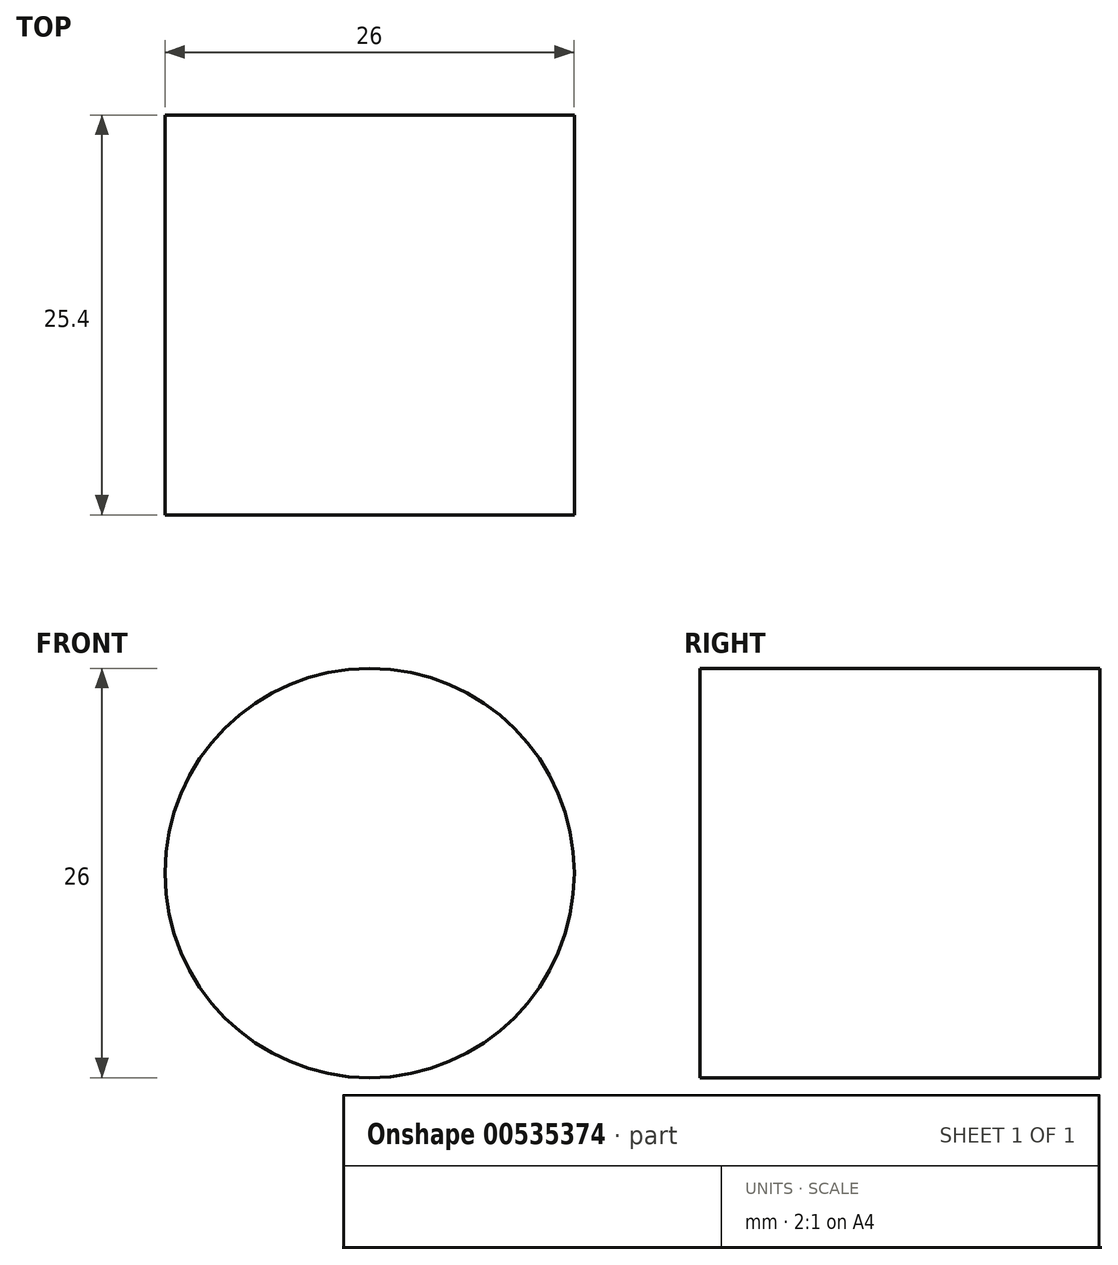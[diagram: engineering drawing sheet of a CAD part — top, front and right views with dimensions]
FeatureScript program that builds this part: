
annotation { "Feature Type Name" : "Feature", "Feature Type Description" : "" }
export const myFeature = defineFeature(function(context is Context, id is Id, definition is map)
    precondition{}
    {
        {
            var Q0;
            Q0=qCreatedBy(makeId("Front.planeOp"),FACE);
            var sketch = newSketch(context, id + "F0", { "sketchPlane" : qUnion([Q0])});
            skCircle(sketch, "E0", {"center": v(0, 0) * mm, "radius": 13 * mm});
            skSolve(sketch);
        }
        {
            var Q0;
            Q0=makeQuery(id+"F0.imprint","IMPRINT",FACE,{"disambiguationData":[TD([[makeQuery(id+"F0.imprint","IMPRINT",EDGE,{"derivedFrom":sQuery(id+"F0.wireOp",EDGE,"E0")}),1.0]])]});
            extrude(context, id + "F1", {"entities" : qUnion([Q0]), "depth" : 25.4 * mm, "offsetDistance" : 25.4 * mm});
        }
    });
